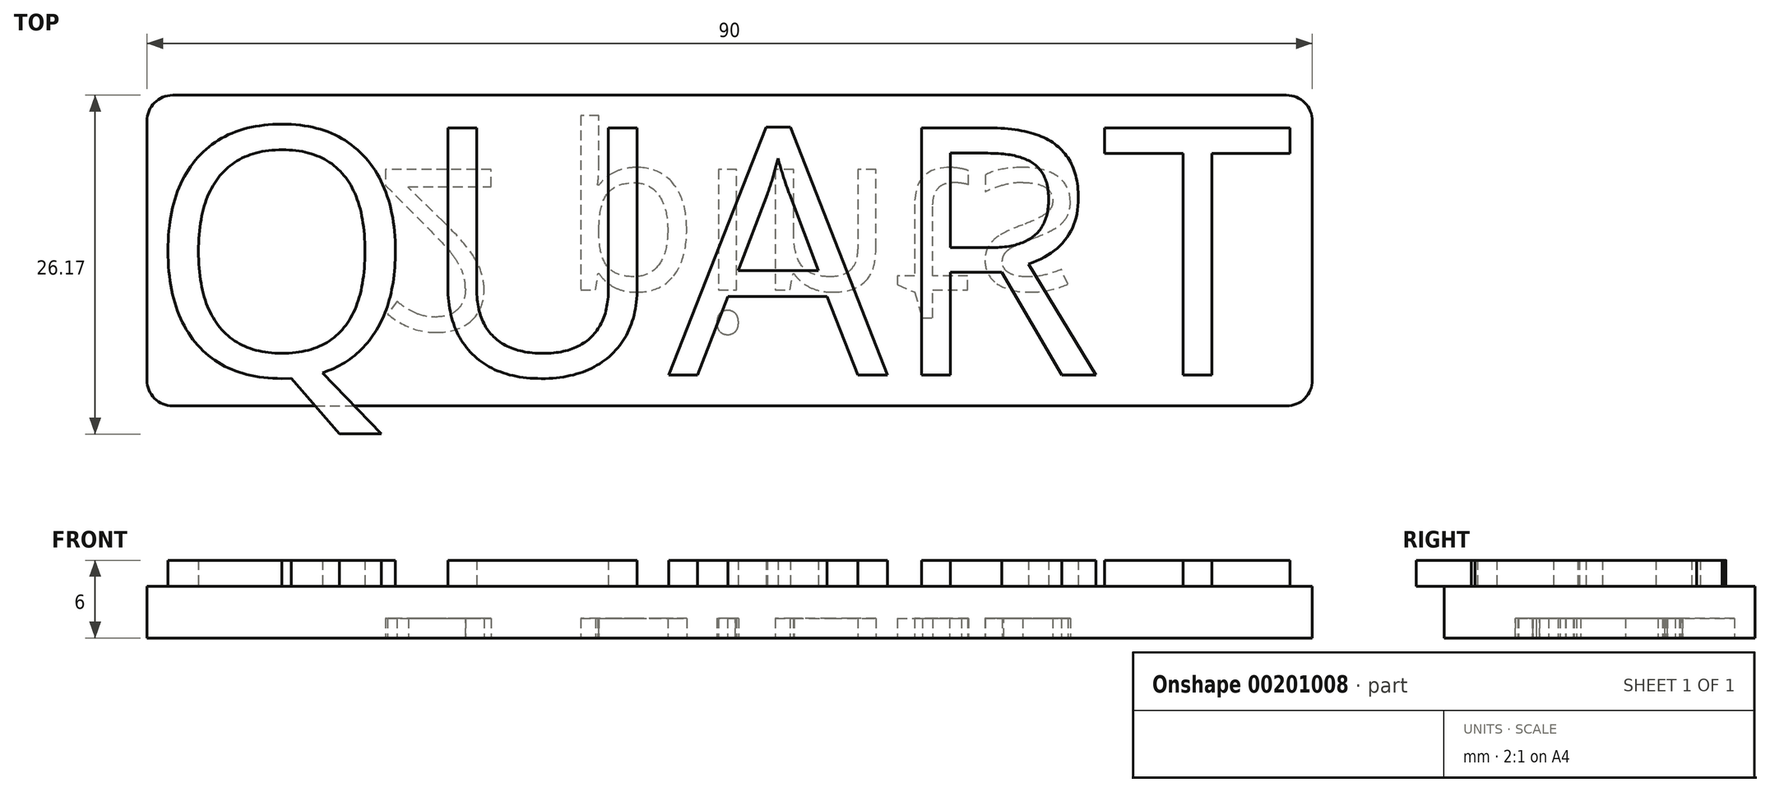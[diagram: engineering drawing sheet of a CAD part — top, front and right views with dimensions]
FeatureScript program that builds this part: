
annotation { "Feature Type Name" : "Feature", "Feature Type Description" : "" }
export const myFeature = defineFeature(function(context is Context, id is Id, definition is map)
    precondition{}
    {
        {
            var Q0;
            Q0=qCreatedBy(makeId("Top.planeOp"),FACE);
            var sketch = newSketch(context, id + "F0", { "sketchPlane" : qUnion([Q0])});
            skLineSegment(sketch, "E0.bottom", {"start": v(-45, 12) * mm, "end": v(45, 12) * mm});
            skLineSegment(sketch, "E0.top", {"start": v(-45, -12) * mm, "end": v(45, -12) * mm});
            skLineSegment(sketch, "E0.left", {"start": v(-45, 12) * mm, "end": v(-45, -12) * mm});
            skLineSegment(sketch, "E0.right", {"start": v(45, 12) * mm, "end": v(45, -12) * mm});
            skLineSegment(sketch, "E1", {"start": v(0, -12) * mm, "end": v(0, 12) * mm, "construction": true});
            skSolve(sketch);
        }
        {
            var Q0;
            Q0=makeQuery(id+"F0.imprint","IMPRINT",FACE,{"disambiguationData":[TD([[makeQuery(id+"F0.imprint","IMPRINT",EDGE,{"derivedFrom":sQuery(id+"F0.wireOp",EDGE,"E0.bottom")}),-1.0]])]});
            extrude(context, id + "F1", {"entities" : qUnion([Q0]), "depth" : 4 * mm});
        }
        {
            var Q0;
            Q0=makeQuery(id+"F1.opExtrude","SWEPT_EDGE",EDGE,{"disambiguationData":[OSD([sQuery(id+"F0.wireOp",EDGE,"E0.top"),sQuery(id+"F0.wireOp",EDGE,"E0.left")])]});
            var Q1;
            Q1=makeQuery(id+"F1.opExtrude","SWEPT_EDGE",EDGE,{"disambiguationData":[OSD([sQuery(id+"F0.wireOp",EDGE,"E0.bottom"),sQuery(id+"F0.wireOp",EDGE,"E0.right")])]});
            var Q2;
            Q2=makeQuery(id+"F1.opExtrude","SWEPT_EDGE",EDGE,{"disambiguationData":[OSD([sQuery(id+"F0.wireOp",EDGE,"E0.bottom"),sQuery(id+"F0.wireOp",EDGE,"E0.left")])]});
            var Q3;
            Q3=makeQuery(id+"F1.opExtrude","SWEPT_EDGE",EDGE,{"disambiguationData":[OSD([sQuery(id+"F0.wireOp",EDGE,"E0.top"),sQuery(id+"F0.wireOp",EDGE,"E0.right")])]});
            fillet(context, id + "F2", {"entities" : qUnion([Q0, Q1, Q2, Q3]), "radius" : 2 * mm, "tangentPropagation" : true, "allowEdgeOverflow" : false});
        }
        {
            var Q0;
            Q0=makeQuery(id+"F1.opExtrude","CAP_FACE",FACE,{"disambiguationData":[OSD([sQuery(id+"F0.wireOp",EDGE,"E0.bottom"),sQuery(id+"F0.wireOp",EDGE,"E0.top"),sQuery(id+"F0.wireOp",EDGE,"E0.left"),sQuery(id+"F0.wireOp",EDGE,"E0.right")])],"isStart":false});
            var sketch = newSketch(context, id + "F3", { "sketchPlane" : qUnion([Q0])});
            skText(sketch, "E2", { "text": "QUART", "fontName": "OpenSans-Regular.ttf"});
            const initialGuessF3  = {"E2": [-0.045, -0.00962, 1, 0, 0.01925]};
            skSetInitialGuess(sketch, initialGuessF3);
            skSolve(sketch);
        }
        {
            var Q0;
            {var subQ0=sQuery(id+"F3.wireOp",EDGE,"E2.sketch_text.stroke-4");Q0=makeQuery(id+"F3.imprint","IMPRINT",FACE,{"disambiguationData":[TD([[makeQuery(id+"F3.imprint","IMPRINT",EDGE,{"derivedFrom":subQ0}),-1.0]])]});}
            var Q1;
            {var subQ0=sQuery(id+"F3.wireOp",EDGE,"E2.sketch_text.stroke-3");var subQ1=sQuery(id+"F3.wireOp",EDGE,"E2.sketch_text.stroke-2");var subQ2=makeQuery(id+"F3.imprint","INTERSECT",VERTEX,{"derivedFrom":[subQ1,subQ0]});Q1=makeQuery(id+"F3.imprint","IMPRINT",FACE,{"disambiguationData":[TD([[makeQuery(id+"F3.imprint","IMPRINT",EDGE,{"disambiguationData":[TD([[subQ2,1.0]])],"derivedFrom":subQ1}),-1.0]])]});}
            var Q2;
            {var subQ1=sQuery(id+"F3.wireOp",EDGE,"E2.sketch_text.stroke-1");Q2=makeQuery(id+"F3.imprint","IMPRINT",FACE,{"disambiguationData":[TD([[makeQuery(id+"F3.imprint","IMPRINT",EDGE,{"derivedFrom":subQ1}),-1.0]])]});}
            var Q3;
            {var subQ0=sQuery(id+"F3.wireOp",EDGE,"E2.sketch_text.stroke-0");var subQ1=makeQuery(id+"F1.opExtrude","CAP_EDGE",EDGE,{"disambiguationData":[OSD([sQuery(id+"F0.wireOp",EDGE,"E0.top")])],"isStart":false});var subQ2=makeQuery(id+"F3.imprint","INTERSECT",VERTEX,{"derivedFrom":[subQ1,subQ0]});Q3=makeQuery(id+"F3.imprint","IMPRINT",FACE,{"disambiguationData":[TD([[makeQuery(id+"F3.imprint","IMPRINT",EDGE,{"disambiguationData":[TD([[subQ2,-1.0]])],"derivedFrom":subQ0}),-1.0]])]});}
            var Q4;
            {var subQ1=sQuery(id+"F3.wireOp",EDGE,"E2.sketch_text.stroke-8");Q4=makeQuery(id+"F3.imprint","IMPRINT",FACE,{"disambiguationData":[TD([[makeQuery(id+"F3.imprint","IMPRINT",EDGE,{"derivedFrom":subQ1}),-1.0]])]});}
            var Q5;
            {var subQ0=sQuery(id+"F3.wireOp",EDGE,"E2.sketch_text.stroke-9");var subQ1=makeQuery(id+"F1.opExtrude","CAP_EDGE",EDGE,{"disambiguationData":[OSD([sQuery(id+"F0.wireOp",EDGE,"E0.bottom")])],"isStart":false});var subQ2=makeQuery(id+"F3.imprint","INTERSECT",VERTEX,{"derivedFrom":[subQ1,subQ0]});Q5=makeQuery(id+"F3.imprint","IMPRINT",FACE,{"disambiguationData":[TD([[makeQuery(id+"F3.imprint","IMPRINT",EDGE,{"disambiguationData":[TD([[subQ2,1.0]])],"derivedFrom":subQ0}),-1.0]])]});}
            var Q6;
            {var subQ1=sQuery(id+"F3.wireOp",EDGE,"E2.sketch_text.stroke-10");Q6=makeQuery(id+"F3.imprint","IMPRINT",FACE,{"disambiguationData":[TD([[makeQuery(id+"F3.imprint","IMPRINT",EDGE,{"derivedFrom":subQ1}),-1.0]])]});}
            var Q7;
            {var subQ0=sQuery(id+"F3.wireOp",EDGE,"E2.sketch_text.stroke-11");var subQ1=makeQuery(id+"F1.opExtrude","CAP_EDGE",EDGE,{"disambiguationData":[OSD([sQuery(id+"F0.wireOp",EDGE,"E0.bottom")])],"isStart":false});var subQ2=makeQuery(id+"F3.imprint","INTERSECT",VERTEX,{"derivedFrom":[subQ1,subQ0]});Q7=makeQuery(id+"F3.imprint","IMPRINT",FACE,{"disambiguationData":[TD([[makeQuery(id+"F3.imprint","IMPRINT",EDGE,{"disambiguationData":[TD([[subQ2,-1.0]])],"derivedFrom":subQ0}),-1.0]])]});}
            var Q8;
            {var subQ0=sQuery(id+"F3.wireOp",EDGE,"E2.sketch_text.stroke-12");Q8=makeQuery(id+"F3.imprint","IMPRINT",FACE,{"disambiguationData":[TD([[makeQuery(id+"F3.imprint","IMPRINT",EDGE,{"derivedFrom":subQ0}),-1.0]])]});}
            var Q9;
            {var subQ0=sQuery(id+"F3.wireOp",EDGE,"E2.sketch_text.stroke-21");Q9=makeQuery(id+"F3.imprint","IMPRINT",FACE,{"disambiguationData":[TD([[makeQuery(id+"F3.imprint","IMPRINT",EDGE,{"derivedFrom":subQ0}),-1.0]])]});}
            var Q10;
            {var subQ0=sQuery(id+"F3.wireOp",EDGE,"E2.sketch_text.stroke-18");var subQ1=makeQuery(id+"F1.opExtrude","CAP_EDGE",EDGE,{"disambiguationData":[OSD([sQuery(id+"F0.wireOp",EDGE,"E0.top")])],"isStart":false});var subQ2=makeQuery(id+"F3.imprint","INTERSECT",VERTEX,{"derivedFrom":[subQ1,subQ0]});Q10=makeQuery(id+"F3.imprint","IMPRINT",FACE,{"disambiguationData":[TD([[makeQuery(id+"F3.imprint","IMPRINT",EDGE,{"disambiguationData":[TD([[subQ2,-1.0]])],"derivedFrom":subQ0}),-1.0]])]});}
            var Q11;
            {var subQ0=sQuery(id+"F3.wireOp",EDGE,"E2.sketch_text.stroke-19");Q11=makeQuery(id+"F3.imprint","IMPRINT",FACE,{"disambiguationData":[TD([[makeQuery(id+"F3.imprint","IMPRINT",EDGE,{"derivedFrom":subQ0}),-1.0]])]});}
            var Q12;
            {var subQ0=sQuery(id+"F3.wireOp",EDGE,"E2.sketch_text.stroke-25");Q12=makeQuery(id+"F3.imprint","IMPRINT",FACE,{"disambiguationData":[TD([[makeQuery(id+"F3.imprint","IMPRINT",EDGE,{"derivedFrom":subQ0}),-1.0]])]});}
            var Q13;
            {var subQ0=sQuery(id+"F3.wireOp",EDGE,"E2.sketch_text.stroke-22");var subQ1=makeQuery(id+"F1.opExtrude","CAP_EDGE",EDGE,{"disambiguationData":[OSD([sQuery(id+"F0.wireOp",EDGE,"E0.top")])],"isStart":false});var subQ2=makeQuery(id+"F3.imprint","INTERSECT",VERTEX,{"derivedFrom":[subQ1,subQ0]});Q13=makeQuery(id+"F3.imprint","IMPRINT",FACE,{"disambiguationData":[TD([[makeQuery(id+"F3.imprint","IMPRINT",EDGE,{"disambiguationData":[TD([[subQ2,-1.0]])],"derivedFrom":subQ0}),-1.0]])]});}
            var Q14;
            {var subQ0=sQuery(id+"F3.wireOp",EDGE,"E2.sketch_text.stroke-23");Q14=makeQuery(id+"F3.imprint","IMPRINT",FACE,{"disambiguationData":[TD([[makeQuery(id+"F3.imprint","IMPRINT",EDGE,{"derivedFrom":subQ0}),-1.0]])]});}
            var Q15;
            {var subQ5=sQuery(id+"F3.wireOp",EDGE,"E2.sketch_text.stroke-28");Q15=makeQuery(id+"F3.imprint","IMPRINT",FACE,{"disambiguationData":[TD([[makeQuery(id+"F3.imprint","IMPRINT",EDGE,{"derivedFrom":subQ5}),-1.0]])]});}
            var Q16;
            {var subQ0=sQuery(id+"F3.wireOp",EDGE,"E2.sketch_text.stroke-34");Q16=makeQuery(id+"F3.imprint","IMPRINT",FACE,{"disambiguationData":[TD([[makeQuery(id+"F3.imprint","IMPRINT",EDGE,{"derivedFrom":subQ0}),-1.0]])]});}
            var Q17;
            {var subQ0=sQuery(id+"F3.wireOp",EDGE,"E2.sketch_text.stroke-30");Q17=makeQuery(id+"F3.imprint","IMPRINT",FACE,{"disambiguationData":[TD([[makeQuery(id+"F3.imprint","IMPRINT",EDGE,{"derivedFrom":subQ0}),-1.0]])]});}
            var Q18;
            {var subQ0=sQuery(id+"F3.wireOp",EDGE,"E2.sketch_text.stroke-6");Q18=makeQuery(id+"F3.imprint","IMPRINT",FACE,{"disambiguationData":[TD([[makeQuery(id+"F3.imprint","IMPRINT",EDGE,{"derivedFrom":subQ0}),-1.0]])]});}
            var Q19;
            {var subQ0=sQuery(id+"F3.wireOp",EDGE,"E2.sketch_text.stroke-17");Q19=makeQuery(id+"F3.imprint","IMPRINT",FACE,{"disambiguationData":[TD([[makeQuery(id+"F3.imprint","IMPRINT",EDGE,{"derivedFrom":subQ0}),-1.0]])]});}
            var Q20;
            {var subQ0=sQuery(id+"F3.wireOp",EDGE,"E2.sketch_text.stroke-27");Q20=makeQuery(id+"F3.imprint","IMPRINT",FACE,{"disambiguationData":[TD([[makeQuery(id+"F3.imprint","IMPRINT",EDGE,{"derivedFrom":subQ0}),-1.0]])]});}
            var Q21;
            Q21=makeQuery(id+"F3.imprint","IMPRINT",FACE,{"disambiguationData":[TD([[makeQuery(id+"F3.imprint","IMPRINT",EDGE,{"derivedFrom":sQuery(id+"F3.wireOp",EDGE,"E2.sketch_text.stroke-47")}),-1.0]])]});
            var Q22;
            Q22=makeQuery(id+"F3.imprint","IMPRINT",FACE,{"disambiguationData":[TD([[makeQuery(id+"F3.imprint","IMPRINT",EDGE,{"derivedFrom":sQuery(id+"F3.wireOp",EDGE,"E2.sketch_text.stroke-65")}),-1.0]])]});
            extrude(context, id + "F4", {"entities" : qUnion([Q0, Q1, Q2, Q3, Q4, Q5, Q6, Q7, Q8, Q9, Q10, Q11, Q12, Q13, Q14, Q15, Q16, Q17, Q18, Q19, Q20, Q21, Q22]), "operationType" : NewBodyOperationType.ADD, "depth" : 2 * mm});
        }
        {
            var Q0;
            Q0=makeQuery(id+"F1.opExtrude","CAP_FACE",FACE,{"disambiguationData":[OSD([sQuery(id+"F0.wireOp",EDGE,"E0.bottom"),sQuery(id+"F0.wireOp",EDGE,"E0.top"),sQuery(id+"F0.wireOp",EDGE,"E0.left"),sQuery(id+"F0.wireOp",EDGE,"E0.right")])],"isStart":true});
            var sketch = newSketch(context, id + "F5", { "sketchPlane" : qUnion([Q0])});
            skText(sketch, "E3", { "text": "2 pints", "fontName": "OpenSans-Regular.ttf"});
            const initialGuessF5  = {"E3": [-0.02743, -0.00625, 1, 0, 0.0125]};
            skSetInitialGuess(sketch, initialGuessF5);
            skSolve(sketch);
        }
        {
            var Q0;
            Q0=makeQuery(id+"F5.imprint","IMPRINT",FACE,{"disambiguationData":[TD([[makeQuery(id+"F5.imprint","IMPRINT",EDGE,{"derivedFrom":sQuery(id+"F5.wireOp",EDGE,"E3.sketch_text.stroke-103")}),-1.0]])]});
            var Q1;
            Q1=makeQuery(id+"F5.imprint","IMPRINT",FACE,{"disambiguationData":[TD([[makeQuery(id+"F5.imprint","IMPRINT",EDGE,{"derivedFrom":sQuery(id+"F5.wireOp",EDGE,"E3.sketch_text.stroke-86")}),-1.0]])]});
            var Q2;
            Q2=makeQuery(id+"F5.imprint","IMPRINT",FACE,{"disambiguationData":[TD([[makeQuery(id+"F5.imprint","IMPRINT",EDGE,{"derivedFrom":sQuery(id+"F5.wireOp",EDGE,"E3.sketch_text.stroke-70")}),-1.0]])]});
            var Q3;
            Q3=makeQuery(id+"F5.imprint","IMPRINT",FACE,{"disambiguationData":[TD([[makeQuery(id+"F5.imprint","IMPRINT",EDGE,{"derivedFrom":sQuery(id+"F5.wireOp",EDGE,"E3.sketch_text.stroke-39")}),-1.0]])]});
            var Q4;
            Q4=makeQuery(id+"F5.imprint","IMPRINT",FACE,{"disambiguationData":[TD([[makeQuery(id+"F5.imprint","IMPRINT",EDGE,{"derivedFrom":sQuery(id+"F5.wireOp",EDGE,"E3.sketch_text.stroke-19")}),-1.0]])]});
            var Q5;
            Q5=makeQuery(id+"F5.imprint","IMPRINT",FACE,{"disambiguationData":[TD([[makeQuery(id+"F5.imprint","IMPRINT",EDGE,{"derivedFrom":sQuery(id+"F5.wireOp",EDGE,"E3.sketch_text.stroke-0")}),-1.0]])]});
            var Q6;
            Q6=makeQuery(id+"F5.imprint","IMPRINT",FACE,{"disambiguationData":[TD([[makeQuery(id+"F5.imprint","IMPRINT",EDGE,{"derivedFrom":sQuery(id+"F5.wireOp",EDGE,"E3.sketch_text.stroke-49")}),-1.0]])]});
            var Q7;
            Q7=makeQuery(id+"F5.imprint","IMPRINT",FACE,{"disambiguationData":[TD([[makeQuery(id+"F5.imprint","IMPRINT",EDGE,{"derivedFrom":sQuery(id+"F5.wireOp",EDGE,"E3.sketch_text.stroke-45")}),-1.0]])]});
            extrude(context, id + "F6", {"entities" : qUnion([Q0, Q1, Q2, Q3, Q4, Q5, Q6, Q7]), "operationType" : NewBodyOperationType.REMOVE, "oppositeDirection" : true, "depth" : 1.5 * mm});
        }
    });
